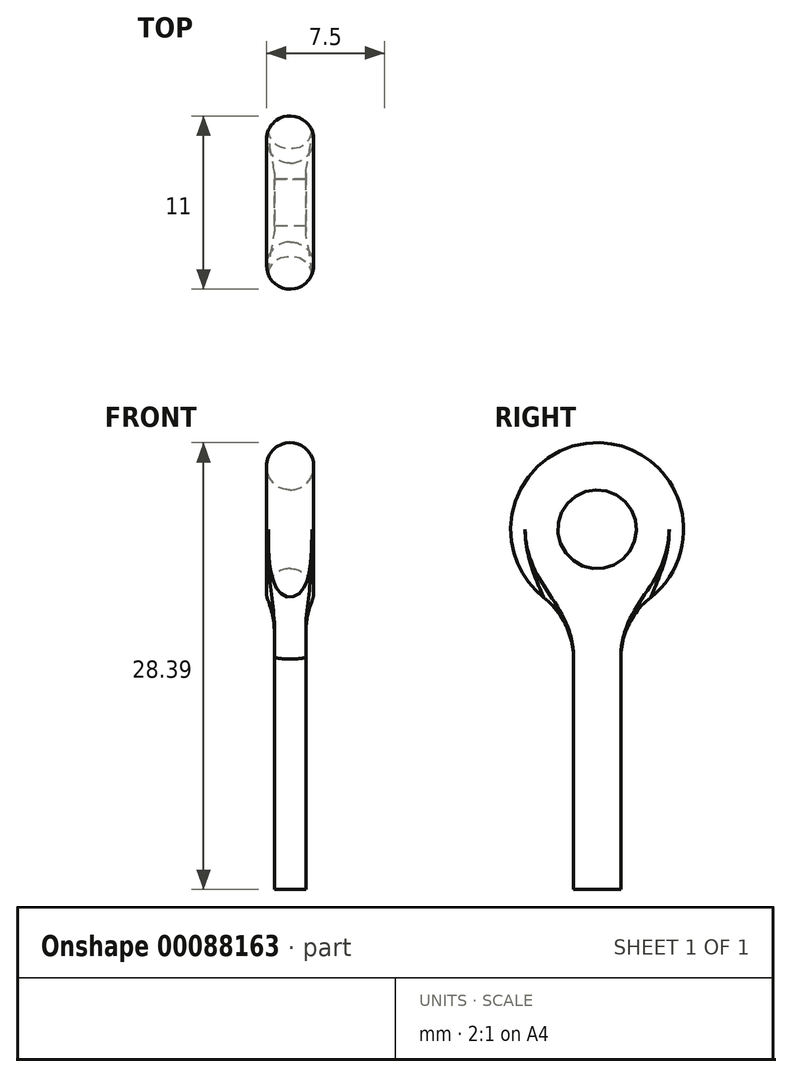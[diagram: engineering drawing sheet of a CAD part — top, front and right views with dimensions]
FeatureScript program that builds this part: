
annotation { "Feature Type Name" : "Feature", "Feature Type Description" : "" }
export const myFeature = defineFeature(function(context is Context, id is Id, definition is map)
    precondition{}
    {
        {
            var Q0;
            Q0=qCreatedBy(makeId("Front.planeOp"),FACE);
            var sketch = newSketch(context, id + "F0", { "sketchPlane" : qUnion([Q0])});
            skLineSegment(sketch, "E0.bottom", {"start": v(0, -9.2) * mm, "end": v(-2, -9.2) * mm});
            skLineSegment(sketch, "E0.top", {"start": v(0, 10.8) * mm, "end": v(-2, 10.8) * mm});
            skLineSegment(sketch, "E0.left", {"start": v(0, -9.2) * mm, "end": v(0, 10.8) * mm});
            skLineSegment(sketch, "E0.right", {"start": v(-2, -9.2) * mm, "end": v(-2, 10.8) * mm});
            skSolve(sketch);
        }
        {
            var Q0;
            Q0=makeQuery(id+"F0.imprint","IMPRINT",FACE,{"disambiguationData":[TD([[makeQuery(id+"F0.imprint","IMPRINT",EDGE,{"derivedFrom":sQuery(id+"F0.wireOp",EDGE,"E0.bottom")}),-1.0]])]});
            extrude(context, id + "F1", {"entities" : qUnion([Q0]), "endBound" : BoundingType.SYMMETRIC, "depth" : 3 * mm});
        }
        {
            var Q0;
            Q0=qCreatedBy(makeId("Front.planeOp"),FACE);
            var sketch = newSketch(context, id + "F2", { "sketchPlane" : qUnion([Q0])});
            skCircle(sketch, "E1", {"center": v(-1, 9.69) * mm, "radius": 1.5 * mm});
            skLineSegment(sketch, "E2", {"start": v(-1, 10.8) * mm, "end": v(-1, 9.69) * mm, "construction": true});
            skLineSegment(sketch, "E3", {"start": v(-1, 11.19) * mm, "end": v(-1, 13.69) * mm, "construction": true});
            skLineSegment(sketch, "E4", {"start": v(-1, 13.69) * mm, "end": v(2.57, 13.69) * mm, "construction": true});
            skSolve(sketch);
        }
        {
            var Q0;
            Q0 = qSketchRegion(id + "F2", true);
            var Q1;
            Q1=sQuery(id+"F2.wireOp",EDGE,"E4");
            revolve(context, id + "F3", {"operationType" : NewBodyOperationType.ADD, "entities" : qUnion([Q0]), "axis" : qUnion([Q1]), "revolveType" : RevolveType.FULL});
        }
        {
            var Q0;
            Q0=makeQuery(id+"F3.boolean.opBoolean","INTERSECT",EDGE,{"derivedFrom":[makeQuery(id+"F1.opExtrude","SWEPT_FACE",FACE,{"disambiguationData":[OSD([sQuery(id+"F0.wireOp",EDGE,"E0.left")])]}),makeQuery(id+"F3.opRevolve","SWEPT_FACE",FACE,{"disambiguationData":[OSD([sQuery(id+"F2.wireOp",EDGE,"E1")])]})]});
            var Q1;
            Q1=makeQuery(id+"F3.boolean.opBoolean","INTERSECT",EDGE,{"derivedFrom":[makeQuery(id+"F1.opExtrude","CAP_FACE",FACE,{"disambiguationData":[OSD([sQuery(id+"F0.wireOp",EDGE,"E0.bottom"),sQuery(id+"F0.wireOp",EDGE,"E0.top"),sQuery(id+"F0.wireOp",EDGE,"E0.left"),sQuery(id+"F0.wireOp",EDGE,"E0.right")])],"isStart":false}),makeQuery(id+"F3.opRevolve","SWEPT_FACE",FACE,{"disambiguationData":[OSD([sQuery(id+"F2.wireOp",EDGE,"E1")])]})]});
            var Q2;
            Q2=makeQuery(id+"F3.boolean.opBoolean","INTERSECT",EDGE,{"derivedFrom":[makeQuery(id+"F1.opExtrude","CAP_FACE",FACE,{"disambiguationData":[OSD([sQuery(id+"F0.wireOp",EDGE,"E0.bottom"),sQuery(id+"F0.wireOp",EDGE,"E0.top"),sQuery(id+"F0.wireOp",EDGE,"E0.left"),sQuery(id+"F0.wireOp",EDGE,"E0.right")])],"isStart":true}),makeQuery(id+"F3.opRevolve","SWEPT_FACE",FACE,{"disambiguationData":[OSD([sQuery(id+"F2.wireOp",EDGE,"E1")])]})]});
            var Q3;
            Q3=makeQuery(id+"F3.boolean.opBoolean","INTERSECT",EDGE,{"derivedFrom":[makeQuery(id+"F1.opExtrude","SWEPT_FACE",FACE,{"disambiguationData":[OSD([sQuery(id+"F0.wireOp",EDGE,"E0.right")])]}),makeQuery(id+"F3.opRevolve","SWEPT_FACE",FACE,{"disambiguationData":[OSD([sQuery(id+"F2.wireOp",EDGE,"E1")])]})]});
            fillet(context, id + "F4", {"entities" : qUnion([Q0, Q1, Q2, Q3]), "radius" : 5 * mm, "tangentPropagation" : true, "allowEdgeOverflow" : false});
        }
    });
